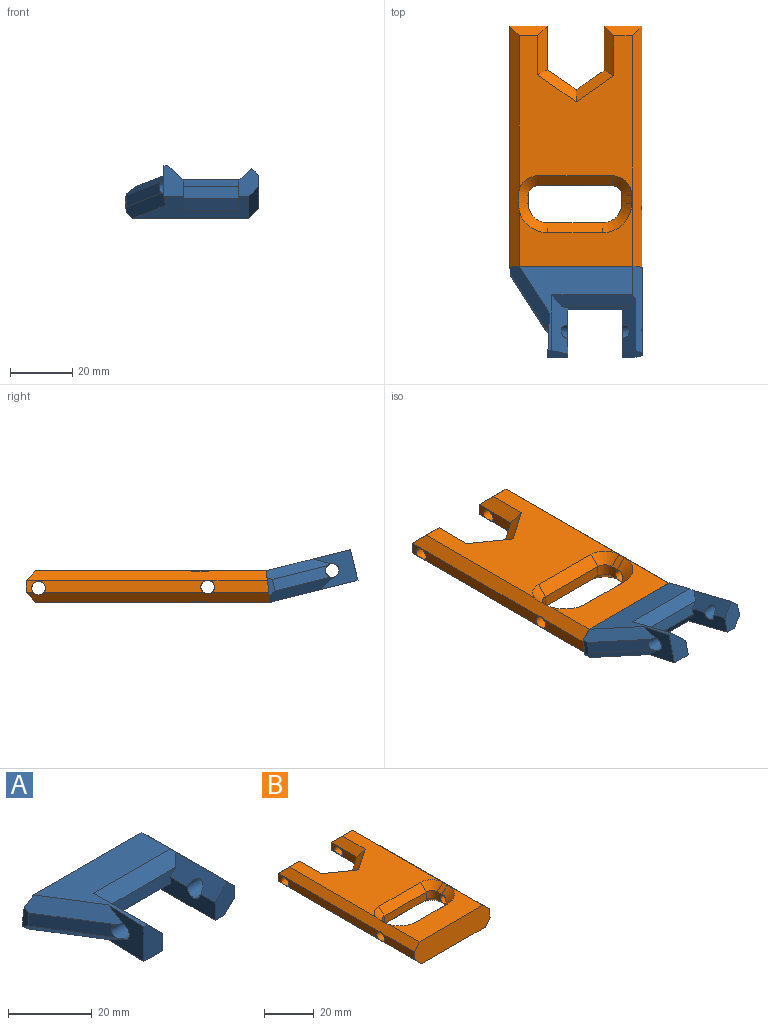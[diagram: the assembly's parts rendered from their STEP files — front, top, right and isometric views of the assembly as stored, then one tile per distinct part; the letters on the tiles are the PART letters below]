
ASSEMBLY  parts=2 mates=1
PART A: 23 faces, bbox 42.7x29.2x10.2 mm
  f0: plane 6.2x3.81mm, normal (1,0,0), area 20.7mm2, adj f6,f14,f15,f16
  f1: plane 12.37x10.16mm, normal (-1,0.04,0), area 81.1mm2, adj f2,f11,f12,f13,f19,f20
  f2: plane 10.16x6.35mm, normal (0,-1,0), area 51.6mm2, adj f1,f3,f11,f12,f22
  f3: plane 18.42x5.08mm, normal (1,0,0), area 74.9mm2, adj f2,f4,f12,f13,f18,f22
  f4: plane 21.59x3.81mm, normal (0,-1,0), area 71.4mm2, adj f3,f5,f17,f18,f21,f22
  f5: plane 18.42x5.08mm, normal (-1,0,0), area 74.9mm2, adj f4,f6,f12,f14,f18,f21
  f6: plane 9.21x6.35mm, normal (0,-1,0), area 42.4mm2, adj f0,f5,f12,f15,f16,f21
  f7: plane 20.42x3.81mm, normal (1,0,0), area 73.9mm2, adj f8,f14,f15,f16
  f8: plane 42.67x10.16mm, normal (0,0.99,0.12), area 421mm2, adj f7,f9,f11,f12,f15,f16,f19,f20
  f9: plane 5.85x2.28mm, normal (-1,0,0), area 9.2mm2, adj f8,f10,f19,f20
  f10: plane 18.28x11.39mm, normal (-0.85,-0.53,0), area 78.6mm2, adj f9,f13,f19,f20
  f11: plane 36.55x27.96mm, normal (0,0,1), area 349.6mm2, adj f1,f2,f8,f16,f17,f20,f22
  f12: plane 37.33x29.21mm, normal (0,0,-1), area 547.7mm2, adj f1,f2,f3,f5,f6,f8,f15,f18
  f13: cylinder r=2.2mm len=7.83mm, axis (1,0,0), area 82.8mm2, adj f1,f3,f10,f19,f20,f22
  f14: cylinder r=2.2mm len=6.35mm, axis (1,0,0), area 77.2mm2, adj f0,f5,f7,f15,f16,f21
  f15: plane 29.21x3.18mm, normal (0.71,0,-0.71), area 129.7mm2, adj f0,f6,f7,f8,f12,f14
  f16: plane 28.35x3.18mm, normal (0.71,0,0.71), area 101.6mm2, adj f0,f6,f7,f8,f11,f14,f17,f21
  f17: plane 26.99x3.18mm, normal (0,-0.71,0.71), area 109.9mm2, adj f4,f11,f16,f21,f22
  f18: plane 17.78x3.18mm, normal (0,-0.71,-0.71), area 79.8mm2, adj f3,f4,f5,f12
  f19: plane 21.97x12.66mm, normal (-0.6,-0.37,-0.71), area 100.3mm2, adj f1,f8,f9,f10,f12,f13
  f20: plane 21.01x12.66mm, normal (-0.6,-0.37,0.71), area 96.8mm2, adj f1,f8,f9,f10,f11,f13
  f21: plane 17.46x4.13mm, normal (-0.71,0,0.71), area 81.7mm2, adj f4,f5,f6,f14,f16,f17
  f22: plane 18.42x5.08mm, normal (0.71,0,0.71), area 105.9mm2, adj f2,f3,f4,f11,f13,f17
PART B: 61 faces, bbox 42.7x78.6x10.2 mm
  f0: plane 57.79x3.81mm, normal (1,0,0), area 202.7mm2, adj f22,f26,f27,f29,f45
  f1: plane 57.79x3.81mm, normal (-1,0,0), area 202.7mm2, adj f12,f25,f28,f39,f55
  f2: cylinder r=6.35mm len=5.97mm, axis (0,0,-1), area 24.7mm2, adj f16,f27,f38,f59
  f3: cylinder r=6.35mm len=0.09mm, axis (0,0,-1), area 0mm2, adj f21,f27,f38
  f4: cylinder r=6.35mm len=0.72mm, axis (0,0,-1), area 0.1mm2, adj f17,f28,f58
  f5: cylinder r=6.35mm len=5.97mm, axis (0,0,-1), area 24.7mm2, adj f16,f28,f37,f58
  f6: cylinder r=6.35mm len=0.09mm, axis (0,0,-1), area 0mm2, adj f17,f28,f37
  f7: cylinder r=6.35mm len=0.72mm, axis (0,0,-1), area 0.1mm2, adj f21,f27,f59
  f8: plane 14.36x3.81mm, normal (-1,0,0), area 41.6mm2, adj f9,f22,f26,f31,f47
  f9: plane 8.94x6.21mm, normal (-0.57,0.82,0), area 41.5mm2, adj f8,f10,f32,f48
  f10: plane 9.34x6.49mm, normal (0.57,0.82,0), area 43.3mm2, adj f9,f11,f33,f49
  f11: plane 14.08x3.81mm, normal (1,0,0), area 40.5mm2, adj f10,f12,f25,f34,f50
  f12: plane 12.19x3.81mm, normal (0,1,0), area 46.5mm2, adj f1,f11,f36,f52
  f13: plane 18.95x3.81mm, normal (-1,0,0), area 67mm2, adj f14,f28,f39,f55
  f14: plane 42.67x10.16mm, normal (0,-0.99,0.12), area 416.5mm2, adj f13,f15,f23,f24,f29,f39,f45,f55
  f15: plane 18.95x3.81mm, normal (1,0,0), area 67mm2, adj f14,f27,f29,f45
  f16: plane 17.55x3.81mm, normal (0,1,0), area 66.9mm2, adj f2,f5,f35,f60
  f17: plane 3.81x2.47mm, normal (1,0,0), area 7.7mm2, adj f4,f6,f18,f28,f40,f56
  f18: cylinder r=3.17mm len=3.81mm, axis (0,0,-1), area 19mm2, adj f17,f19,f42,f53
  f19: plane 23.9x3.81mm, normal (0,-1,0), area 91.1mm2, adj f18,f20,f44,f51
  f20: cylinder r=3.17mm len=3.81mm, axis (0,0,-1), area 19mm2, adj f19,f21,f43,f54
  f21: plane 3.81x2.47mm, normal (-1,0,0), area 7.7mm2, adj f3,f7,f20,f27,f41,f57
  f22: plane 12.19x3.81mm, normal (0,1,0), area 46.5mm2, adj f0,f8,f30,f46
  f23: plane 74.17x36.32mm, normal (0,0,1), area 1662.5mm2, adj f14,f45,f46,f47,f48,f49,f50,f51
  f24: plane 75.42x36.32mm, normal (0,0,-1), area 1707.8mm2, adj f14,f29,f30,f31,f32,f33,f34,f35
  f25: cylinder r=2.2mm len=12.19mm, axis (1,0,0), area 164.1mm2, adj f1,f11,f34,f39
  f26: cylinder r=2.2mm len=12.19mm, axis (1,0,0), area 164.1mm2, adj f0,f8,f29,f31
  f27: cylinder r=2.2mm len=7.57mm, axis (1,0,0), area 91.8mm2, adj f0,f2,f3,f7,f15,f21,f29,f38
  f28: cylinder r=2.2mm len=7.15mm, axis (1,0,0), area 86.1mm2, adj f1,f4,f5,f6,f13,f17,f37,f39
  f29: plane 78.59x3.18mm, normal (0.71,0,-0.71), area 340.7mm2, adj f0,f14,f15,f24,f26,f27,f30
  f30: plane 12.19x3.18mm, normal (0,0.71,-0.71), area 40.5mm2, adj f22,f24,f29,f31
  f31: plane 16.02x3.18mm, normal (-0.71,0,-0.71), area 58.1mm2, adj f8,f24,f26,f30,f32
  f32: plane 12.12x10.08mm, normal (-0.4,0.58,-0.71), area 57.6mm2, adj f9,f24,f31,f33
  f33: plane 12.52x10.35mm, normal (0.4,0.58,-0.71), area 59.8mm2, adj f10,f24,f32,f34
  f34: plane 15.74x3.18mm, normal (0.71,0,-0.71), area 56.9mm2, adj f11,f24,f25,f33,f36
  f35: plane 17.55x3.18mm, normal (0,0.71,-0.71), area 78.8mm2, adj f16,f24,f37,f38
  f36: plane 12.19x3.18mm, normal (0,0.71,-0.71), area 40.5mm2, adj f12,f24,f34,f39
  f37: cone r=9.53mm half-angle=45deg, axis (0,0,-1), area 54.3mm2, adj f5,f6,f24,f28,f35,f39,f40
  f38: cone r=9.53mm half-angle=45deg, axis (0,0,-1), area 54.7mm2, adj f2,f3,f24,f27,f35,f41
  f39: plane 78.59x3.18mm, normal (-0.71,0,-0.71), area 339.4mm2, adj f1,f13,f14,f24,f25,f28,f36,f37
  f40: plane 3x3mm, normal (0.71,0,-0.71), area 10.5mm2, adj f17,f37,f39,f42
  f41: plane 3.18x3.18mm, normal (-0.71,0,-0.71), area 11.1mm2, adj f21,f24,f38,f43
  f42: cone r=6.35mm half-angle=45deg, axis (0,0,-1), area 33.2mm2, adj f18,f24,f39,f40,f44
  f43: cone r=6.35mm half-angle=45deg, axis (0,0,-1), area 33.6mm2, adj f20,f24,f41,f44
  f44: plane 23.9x3.18mm, normal (0,-0.71,-0.71), area 107.3mm2, adj f19,f24,f42,f43
  f45: plane 77.73x3.18mm, normal (0.71,0,0.71), area 340.9mm2, adj f0,f14,f15,f23,f27,f46
  f46: plane 12.19x3.18mm, normal (0,0.71,0.71), area 40.5mm2, adj f22,f23,f45,f47
  f47: plane 16.02x3.18mm, normal (-0.71,0,0.71), area 61.1mm2, adj f8,f23,f46,f48
  f48: plane 12.12x10.08mm, normal (-0.4,0.58,0.71), area 57.6mm2, adj f9,f23,f47,f49
  f49: plane 12.52x10.35mm, normal (0.4,0.58,0.71), area 59.8mm2, adj f10,f23,f48,f50
  f50: plane 15.74x3.18mm, normal (0.71,0,0.71), area 59.8mm2, adj f11,f23,f49,f52
  f51: plane 23.9x3.18mm, normal (0,-0.71,0.71), area 107.3mm2, adj f19,f23,f53,f54
  f52: plane 12.19x3.18mm, normal (0,0.71,0.71), area 40.5mm2, adj f12,f23,f50,f55
  f53: cone r=3.17mm half-angle=45deg, axis (0,0,1), area 33.2mm2, adj f18,f23,f51,f55,f56
  f54: cone r=3.17mm half-angle=45deg, axis (0,0,1), area 33.6mm2, adj f20,f23,f51,f57
  f55: plane 77.73x3.18mm, normal (-0.71,0,0.71), area 339.5mm2, adj f1,f13,f14,f23,f28,f52,f53,f56
  f56: plane 3x3mm, normal (0.71,0,0.71), area 10.5mm2, adj f17,f53,f55,f58
  f57: plane 3.18x3.18mm, normal (-0.71,0,0.71), area 11.1mm2, adj f21,f23,f54,f59
  f58: cone r=6.35mm half-angle=45deg, axis (0,0,1), area 55.4mm2, adj f4,f5,f23,f28,f55,f56,f60
  f59: cone r=6.35mm half-angle=45deg, axis (0,0,1), area 55.8mm2, adj f2,f7,f23,f27,f57,f60
  f60: plane 17.55x3.18mm, normal (0,0.71,0.71), area 78.8mm2, adj f16,f23,f58,f59
PLACE A rot(axis=(-1,0,0),14deg) t=(-13.36,-69.89,10.59)mm
PLACE B t=(-14.17,-2.24,5.42)mm
MATE fastened A.f8 <-> B.f14  axis (0,0.99,-0.12) through (-17.53,-48.58,10.5)mm
